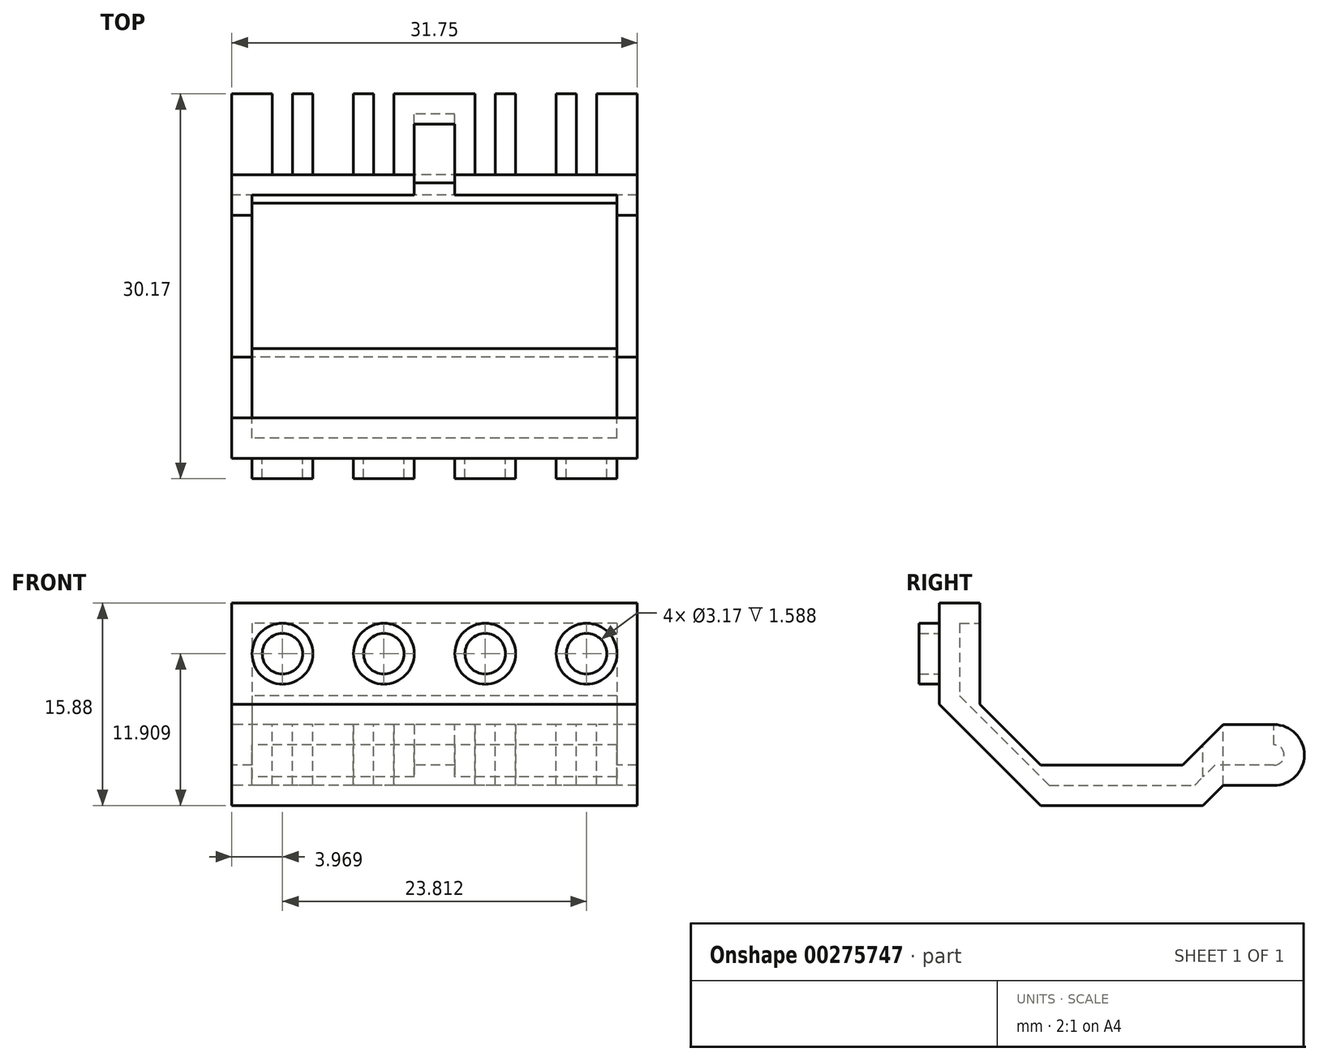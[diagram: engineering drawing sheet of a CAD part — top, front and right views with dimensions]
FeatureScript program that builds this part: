
annotation { "Feature Type Name" : "Feature", "Feature Type Description" : "" }
export const myFeature = defineFeature(function(context is Context, id is Id, definition is map)
    precondition{}
    {
        {
            var Q0;
            Q0=qCreatedBy(makeId("Right.planeOp"),FACE);
            var sketch = newSketch(context, id + "F0", { "sketchPlane" : qUnion([Q0])});
            skLineSegment(sketch, "E0.bottom", {"start": v(-14.29, 7.94) * mm, "end": v(14.29, 7.94) * mm});
            skLineSegment(sketch, "E0.top", {"start": v(-14.29, -7.94) * mm, "end": v(14.29, -7.94) * mm});
            skLineSegment(sketch, "E0.left", {"start": v(-14.29, 7.94) * mm, "end": v(-14.29, -7.94) * mm});
            skLineSegment(sketch, "E0.right", {"start": v(14.29, 7.94) * mm, "end": v(14.29, -7.94) * mm});
            skPoint(sketch, "E0.middle", {"position": v(0, 0) * mm});
            skPoint(sketch, "E1", {"position": v(-11.11, 7.94) * mm});
            skPoint(sketch, "E2", {"position": v(-14.29, 0) * mm});
            skLineSegment(sketch, "E3", {"start": v(-14.29, 0) * mm, "end": v(-6.35, -7.94) * mm});
            skLineSegment(sketch, "E4", {"start": v(-11.11, 7.94) * mm, "end": v(-11.11, 0) * mm});
            skPoint(sketch, "E5", {"position": v(6.35, -7.94) * mm});
            skLineSegment(sketch, "E6", {"start": v(-11.11, 0) * mm, "end": v(-6.35, -4.76) * mm});
            skPoint(sketch, "E7", {"position": v(4.76, -4.76) * mm});
            skLineSegment(sketch, "E8", {"start": v(-6.35, -4.76) * mm, "end": v(4.76, -4.76) * mm});
            skLineSegment(sketch, "E9", {"start": v(4.76, -4.76) * mm, "end": v(14.29, 4.76) * mm});
            skPoint(sketch, "E10", {"position": v(7.94, -6.35) * mm});
            skPoint(sketch, "E11", {"position": v(7.94, -1.59) * mm});
            skLineSegment(sketch, "E12", {"start": v(7.94, -6.35) * mm, "end": v(14.29, -6.35) * mm});
            skLineSegment(sketch, "E13", {"start": v(6.35, -7.94) * mm, "end": v(7.94, -6.35) * mm});
            skLineSegment(sketch, "E14", {"start": v(7.94, -1.59) * mm, "end": v(14.29, -1.59) * mm});
            skLineSegment(sketch, "E15", {"start": v(7.94, -1.59) * mm, "end": v(7.94, -6.35) * mm});
            skLineSegment(sketch, "E16", {"start": v(-6.35, -4.76) * mm, "end": v(-6.35, -7.94) * mm});
            skPoint(sketch, "E17", {"position": v(14.29, -3.97) * mm});
            skLineSegment(sketch, "E18", {"start": v(14.29, -3.97) * mm, "end": v(11.9, -3.97) * mm});
            skCircle(sketch, "E19", {"center": v(11.9, -3.97) * mm, "radius": 2.38 * mm});
            skSolve(sketch);
        }
        {
            var Q0;
            {var subQ1=sQuery(id+"F0.wireOp",EDGE,"E3");Q0=makeQuery(id+"F0.imprint","IMPRINT",FACE,{"disambiguationData":[TD([[makeQuery(id+"F0.imprint","IMPRINT",EDGE,{"derivedFrom":subQ1}),1.0]])]});}
            var Q1;
            {var subQ1=sQuery(id+"F0.wireOp",EDGE,"E8");Q1=makeQuery(id+"F0.imprint","IMPRINT",FACE,{"disambiguationData":[TD([[makeQuery(id+"F0.imprint","IMPRINT",EDGE,{"derivedFrom":subQ1}),-1.0]])]});}
            var Q2;
            {var subQ0=sQuery(id+"F0.wireOp",EDGE,"E15");Q2=makeQuery(id+"F0.imprint","IMPRINT",FACE,{"disambiguationData":[TD([[makeQuery(id+"F0.imprint","IMPRINT",EDGE,{"derivedFrom":subQ0}),1.0]])]});}
            var Q3;
            {var subQ0=sQuery(id+"F0.wireOp",EDGE,"E19");var subQ1=makeQuery(id+"F0.imprint","INTERSECT",VERTEX,{"derivedFrom":[sQuery(id+"F0.wireOp",EDGE,"E0.right"),subQ0]});Q3=makeQuery(id+"F0.imprint","IMPRINT",FACE,{"disambiguationData":[TD([[makeQuery(id+"F0.imprint","IMPRINT",EDGE,{"disambiguationData":[TD([[subQ1,-1.0]])],"derivedFrom":subQ0}),1.0]])]});}
            extrude(context, id + "F1", {"entities" : qUnion([Q0, Q1, Q2, Q3]), "depth" : 31.75 * mm});
        }
        {
            var Q0;
            Q0=makeQuery(id+"F1.opExtrude","SWEPT_FACE",FACE,{"disambiguationData":[OSD([sQuery(id+"F0.wireOp",EDGE,"E0.left")])]});
            var sketch = newSketch(context, id + "F2", { "sketchPlane" : qUnion([Q0])});
            skCircle(sketch, "E20", {"center": v(3.97, 3.97) * mm, "radius": 2.38 * mm});
            skCircle(sketch, "E21.0", {"center": v(3.97, 3.97) * mm, "radius": 1.59 * mm});
            skCircle(sketch, "E22.1.0.0", {"center": v(11.9, 3.97) * mm, "radius": 2.38 * mm});
            skCircle(sketch, "E22.1.0.1", {"center": v(11.9, 3.97) * mm, "radius": 1.59 * mm});
            skCircle(sketch, "E22.2.0.0", {"center": v(19.84, 3.97) * mm, "radius": 2.38 * mm});
            skCircle(sketch, "E22.2.0.1", {"center": v(19.84, 3.97) * mm, "radius": 1.59 * mm});
            skCircle(sketch, "E22.3.0.0", {"center": v(27.78, 3.97) * mm, "radius": 2.38 * mm});
            skCircle(sketch, "E22.3.0.1", {"center": v(27.78, 3.97) * mm, "radius": 1.59 * mm});
            skLineSegment(sketch, "E22.direction1", {"start": v(3.97, 3.97) * mm, "end": v(11.9, 3.97) * mm, "construction": true});
            skSolve(sketch);
        }
        {
            var Q0;
            Q0=qSketchRegion(id+"F2",true);
            extrude(context, id + "F3", {"entities" : qUnion([Q0]), "operationType" : NewBodyOperationType.ADD, "depth" : 1.59 * mm});
        }
        {
            var Q0;
            Q0=makeQuery(id+"F1.opExtrude","SWEPT_FACE",FACE,{"disambiguationData":[OSD([sQuery(id+"F0.wireOp",EDGE,"E14")])]});
            var sketch = newSketch(context, id + "F4", { "sketchPlane" : qUnion([Q0])});
            skPoint(sketch, "E23", {"position": v(3.18, 7.94) * mm});
            skPoint(sketch, "E24", {"position": v(4.76, 7.94) * mm});
            skPoint(sketch, "E25", {"position": v(6.35, 7.94) * mm});
            skPoint(sketch, "E26", {"position": v(9.53, 7.94) * mm});
            skPoint(sketch, "E27", {"position": v(11.11, 7.94) * mm});
            skPoint(sketch, "E28", {"position": v(12.7, 7.94) * mm});
            skPoint(sketch, "E29.MirrorP", {"position": v(19.05, 7.94) * mm});
            skPoint(sketch, "E30.MirrorP", {"position": v(20.64, 7.94) * mm});
            skPoint(sketch, "E31.MirrorP", {"position": v(22.23, 7.94) * mm});
            skPoint(sketch, "E32.MirrorP", {"position": v(25.4, 7.94) * mm});
            skPoint(sketch, "E33.MirrorP", {"position": v(26.99, 7.94) * mm});
            skPoint(sketch, "E34.MirrorP", {"position": v(28.57, 7.94) * mm});
            skLineSegment(sketch, "E35", {"start": v(3.18, 7.94) * mm, "end": v(3.18, 14.29) * mm});
            skLineSegment(sketch, "E36", {"start": v(4.76, 7.94) * mm, "end": v(4.76, 14.29) * mm});
            skLineSegment(sketch, "E37", {"start": v(3.18, 14.29) * mm, "end": v(4.76, 14.29) * mm});
            skLineSegment(sketch, "E38", {"start": v(6.35, 7.94) * mm, "end": v(6.35, 14.29) * mm});
            skLineSegment(sketch, "E39", {"start": v(6.35, 14.29) * mm, "end": v(9.53, 14.29) * mm});
            skLineSegment(sketch, "E40", {"start": v(9.53, 14.29) * mm, "end": v(9.53, 7.94) * mm});
            skLineSegment(sketch, "E41", {"start": v(11.11, 7.94) * mm, "end": v(11.11, 14.29) * mm});
            skLineSegment(sketch, "E42", {"start": v(11.11, 14.29) * mm, "end": v(12.7, 14.29) * mm});
            skLineSegment(sketch, "E43", {"start": v(12.7, 14.29) * mm, "end": v(12.7, 7.94) * mm});
            skLineSegment(sketch, "E44.MirrorCS", {"start": v(19.05, 14.29) * mm, "end": v(19.05, 7.94) * mm});
            skLineSegment(sketch, "E45.MirrorCS", {"start": v(20.64, 7.94) * mm, "end": v(20.64, 14.29) * mm});
            skLineSegment(sketch, "E46.MirrorCS", {"start": v(20.64, 14.29) * mm, "end": v(19.05, 14.29) * mm});
            skLineSegment(sketch, "E47.MirrorCS", {"start": v(22.23, 14.29) * mm, "end": v(22.23, 7.94) * mm});
            skLineSegment(sketch, "E48.MirrorCS", {"start": v(25.4, 14.29) * mm, "end": v(22.23, 14.29) * mm});
            skLineSegment(sketch, "E49.MirrorCS", {"start": v(25.4, 7.94) * mm, "end": v(25.4, 14.29) * mm});
            skLineSegment(sketch, "E50.MirrorCS", {"start": v(26.99, 7.94) * mm, "end": v(26.99, 14.29) * mm});
            skLineSegment(sketch, "E51.MirrorCS", {"start": v(28.57, 14.29) * mm, "end": v(26.99, 14.29) * mm});
            skLineSegment(sketch, "E52.MirrorCS", {"start": v(28.57, 7.94) * mm, "end": v(28.57, 14.29) * mm});
            skSolve(sketch);
        }
        {
            var Q0;
            {var subQ0=sQuery(id+"F4.wireOp",EDGE,"E37");Q0=makeQuery(id+"F4.imprint","IMPRINT",FACE,{"disambiguationData":[TD([[makeQuery(id+"F4.imprint","IMPRINT",EDGE,{"derivedFrom":subQ0}),-1.0]])]});}
            var Q1;
            {var subQ0=sQuery(id+"F4.wireOp",EDGE,"E35");var subQ1=sQuery(id+"F0.wireOp",EDGE,"E14");var subQ4=makeQuery(id+"F1.opExtrude","SWEPT_EDGE",EDGE,{"disambiguationData":[OSD([subQ1,sQuery(id+"F0.wireOp",EDGE,"E19")])]});var subQ5=makeQuery(id+"F4.imprint","INTERSECT",VERTEX,{"derivedFrom":[subQ4,subQ0]});Q1=makeQuery(id+"F4.imprint","IMPRINT",FACE,{"disambiguationData":[TD([[makeQuery(id+"F4.imprint","IMPRINT",EDGE,{"disambiguationData":[TD([[subQ5,1.0]])],"derivedFrom":subQ0}),-1.0]])]});}
            var Q2;
            {var subQ0=sQuery(id+"F4.wireOp",EDGE,"E38");var subQ1=sQuery(id+"F0.wireOp",EDGE,"E14");var subQ4=makeQuery(id+"F1.opExtrude","SWEPT_EDGE",EDGE,{"disambiguationData":[OSD([subQ1,sQuery(id+"F0.wireOp",EDGE,"E19")])]});var subQ5=makeQuery(id+"F4.imprint","INTERSECT",VERTEX,{"derivedFrom":[subQ4,subQ0]});Q2=makeQuery(id+"F4.imprint","IMPRINT",FACE,{"disambiguationData":[TD([[makeQuery(id+"F4.imprint","IMPRINT",EDGE,{"disambiguationData":[TD([[subQ5,1.0]])],"derivedFrom":subQ0}),-1.0]])]});}
            var Q3;
            {var subQ0=sQuery(id+"F4.wireOp",EDGE,"E39");Q3=makeQuery(id+"F4.imprint","IMPRINT",FACE,{"disambiguationData":[TD([[makeQuery(id+"F4.imprint","IMPRINT",EDGE,{"derivedFrom":subQ0}),-1.0]])]});}
            var Q4;
            {var subQ0=sQuery(id+"F4.wireOp",EDGE,"E42");Q4=makeQuery(id+"F4.imprint","IMPRINT",FACE,{"disambiguationData":[TD([[makeQuery(id+"F4.imprint","IMPRINT",EDGE,{"derivedFrom":subQ0}),-1.0]])]});}
            var Q5;
            {var subQ0=sQuery(id+"F4.wireOp",EDGE,"E41");var subQ1=sQuery(id+"F0.wireOp",EDGE,"E14");var subQ4=makeQuery(id+"F1.opExtrude","SWEPT_EDGE",EDGE,{"disambiguationData":[OSD([subQ1,sQuery(id+"F0.wireOp",EDGE,"E19")])]});var subQ5=makeQuery(id+"F4.imprint","INTERSECT",VERTEX,{"derivedFrom":[subQ4,subQ0]});Q5=makeQuery(id+"F4.imprint","IMPRINT",FACE,{"disambiguationData":[TD([[makeQuery(id+"F4.imprint","IMPRINT",EDGE,{"disambiguationData":[TD([[subQ5,1.0]])],"derivedFrom":subQ0}),-1.0]])]});}
            var Q6;
            {var subQ0=sQuery(id+"F4.wireOp",EDGE,"E44.MirrorCS");var subQ1=sQuery(id+"F0.wireOp",EDGE,"E14");var subQ4=makeQuery(id+"F1.opExtrude","SWEPT_EDGE",EDGE,{"disambiguationData":[OSD([subQ1,sQuery(id+"F0.wireOp",EDGE,"E19")])]});var subQ5=makeQuery(id+"F4.imprint","INTERSECT",VERTEX,{"derivedFrom":[subQ4,subQ0]});Q6=makeQuery(id+"F4.imprint","IMPRINT",FACE,{"disambiguationData":[TD([[makeQuery(id+"F4.imprint","IMPRINT",EDGE,{"disambiguationData":[TD([[subQ5,-1.0]])],"derivedFrom":subQ0}),1.0]])]});}
            var Q7;
            {var subQ0=sQuery(id+"F4.wireOp",EDGE,"E46.MirrorCS");Q7=makeQuery(id+"F4.imprint","IMPRINT",FACE,{"disambiguationData":[TD([[makeQuery(id+"F4.imprint","IMPRINT",EDGE,{"derivedFrom":subQ0}),1.0]])]});}
            var Q8;
            {var subQ0=sQuery(id+"F4.wireOp",EDGE,"E48.MirrorCS");Q8=makeQuery(id+"F4.imprint","IMPRINT",FACE,{"disambiguationData":[TD([[makeQuery(id+"F4.imprint","IMPRINT",EDGE,{"derivedFrom":subQ0}),1.0]])]});}
            var Q9;
            {var subQ0=sQuery(id+"F4.wireOp",EDGE,"E47.MirrorCS");var subQ1=sQuery(id+"F0.wireOp",EDGE,"E14");var subQ4=makeQuery(id+"F1.opExtrude","SWEPT_EDGE",EDGE,{"disambiguationData":[OSD([subQ1,sQuery(id+"F0.wireOp",EDGE,"E19")])]});var subQ5=makeQuery(id+"F4.imprint","INTERSECT",VERTEX,{"derivedFrom":[subQ4,subQ0]});Q9=makeQuery(id+"F4.imprint","IMPRINT",FACE,{"disambiguationData":[TD([[makeQuery(id+"F4.imprint","IMPRINT",EDGE,{"disambiguationData":[TD([[subQ5,-1.0]])],"derivedFrom":subQ0}),1.0]])]});}
            var Q10;
            {var subQ0=sQuery(id+"F4.wireOp",EDGE,"E50.MirrorCS");var subQ1=sQuery(id+"F0.wireOp",EDGE,"E14");var subQ4=makeQuery(id+"F1.opExtrude","SWEPT_EDGE",EDGE,{"disambiguationData":[OSD([subQ1,sQuery(id+"F0.wireOp",EDGE,"E19")])]});var subQ5=makeQuery(id+"F4.imprint","INTERSECT",VERTEX,{"derivedFrom":[subQ4,subQ0]});Q10=makeQuery(id+"F4.imprint","IMPRINT",FACE,{"disambiguationData":[TD([[makeQuery(id+"F4.imprint","IMPRINT",EDGE,{"disambiguationData":[TD([[subQ5,1.0]])],"derivedFrom":subQ0}),-1.0]])]});}
            var Q11;
            {var subQ0=sQuery(id+"F4.wireOp",EDGE,"E51.MirrorCS");Q11=makeQuery(id+"F4.imprint","IMPRINT",FACE,{"disambiguationData":[TD([[makeQuery(id+"F4.imprint","IMPRINT",EDGE,{"derivedFrom":subQ0}),1.0]])]});}
            extrude(context, id + "F5", {"entities" : qUnion([Q0, Q1, Q2, Q3, Q4, Q5, Q6, Q7, Q8, Q9, Q10, Q11]), "operationType" : NewBodyOperationType.REMOVE, "oppositeDirection" : true, "depth" : 25.4 * mm});
        }
        {
            var Q0;
            {var subQ0=sQuery(id+"F4.wireOp",EDGE,"E35");var subQ3=sQuery(id+"F0.wireOp",EDGE,"E14");Q0=makeQuery(id+"F5.boolean.opBoolean","SPLIT",FACE,{"disambiguationData":[TD([makeQuery(id+"F5.opExtrude","SWEPT_FACE",FACE,{"disambiguationData":[OSD([subQ0])]})])],"derivedFrom":makeQuery(id+"F1.opExtrude","SWEPT_FACE",FACE,{"disambiguationData":[OSD([subQ3])]})});}
            var Q1;
            Q1=makeQuery(id+"F1.opExtrude","SWEPT_FACE",FACE,{"disambiguationData":[OSD([sQuery(id+"F0.wireOp",EDGE,"E9")])]});
            var Q2;
            {var subQ1=sQuery(id+"F4.wireOp",EDGE,"E43");var subQ4=sQuery(id+"F0.wireOp",EDGE,"E14");Q2=makeQuery(id+"F5.boolean.opBoolean","SPLIT",FACE,{"disambiguationData":[TD([makeQuery(id+"F5.opExtrude","SWEPT_FACE",FACE,{"disambiguationData":[OSD([subQ1])]})])],"derivedFrom":makeQuery(id+"F1.opExtrude","SWEPT_FACE",FACE,{"disambiguationData":[OSD([subQ4])]})});}
            var Q3;
            {var subQ1=sQuery(id+"F0.wireOp",EDGE,"E14");var subQ3=sQuery(id+"F4.wireOp",EDGE,"E52.MirrorCS");Q3=makeQuery(id+"F5.boolean.opBoolean","SPLIT",FACE,{"disambiguationData":[TD([makeQuery(id+"F5.opExtrude","SWEPT_FACE",FACE,{"disambiguationData":[OSD([subQ3])]})])],"derivedFrom":makeQuery(id+"F1.opExtrude","SWEPT_FACE",FACE,{"disambiguationData":[OSD([subQ1])]})});}
            var Q4;
            Q4=makeQuery(id+"F1.opExtrude","SWEPT_FACE",FACE,{"disambiguationData":[OSD([sQuery(id+"F0.wireOp",EDGE,"E8")])]});
            var Q5;
            Q5=makeQuery(id+"F1.opExtrude","SWEPT_FACE",FACE,{"disambiguationData":[OSD([sQuery(id+"F0.wireOp",EDGE,"E6")])]});
            var Q6;
            Q6=makeQuery(id+"F1.opExtrude","SWEPT_FACE",FACE,{"disambiguationData":[OSD([sQuery(id+"F0.wireOp",EDGE,"E4")])]});
            shell(context, id + "F6", {"entities" : qUnion([Q0, Q1, Q2, Q3, Q4, Q5, Q6]), "thickness" : 1.59 * mm});
        }
    });
